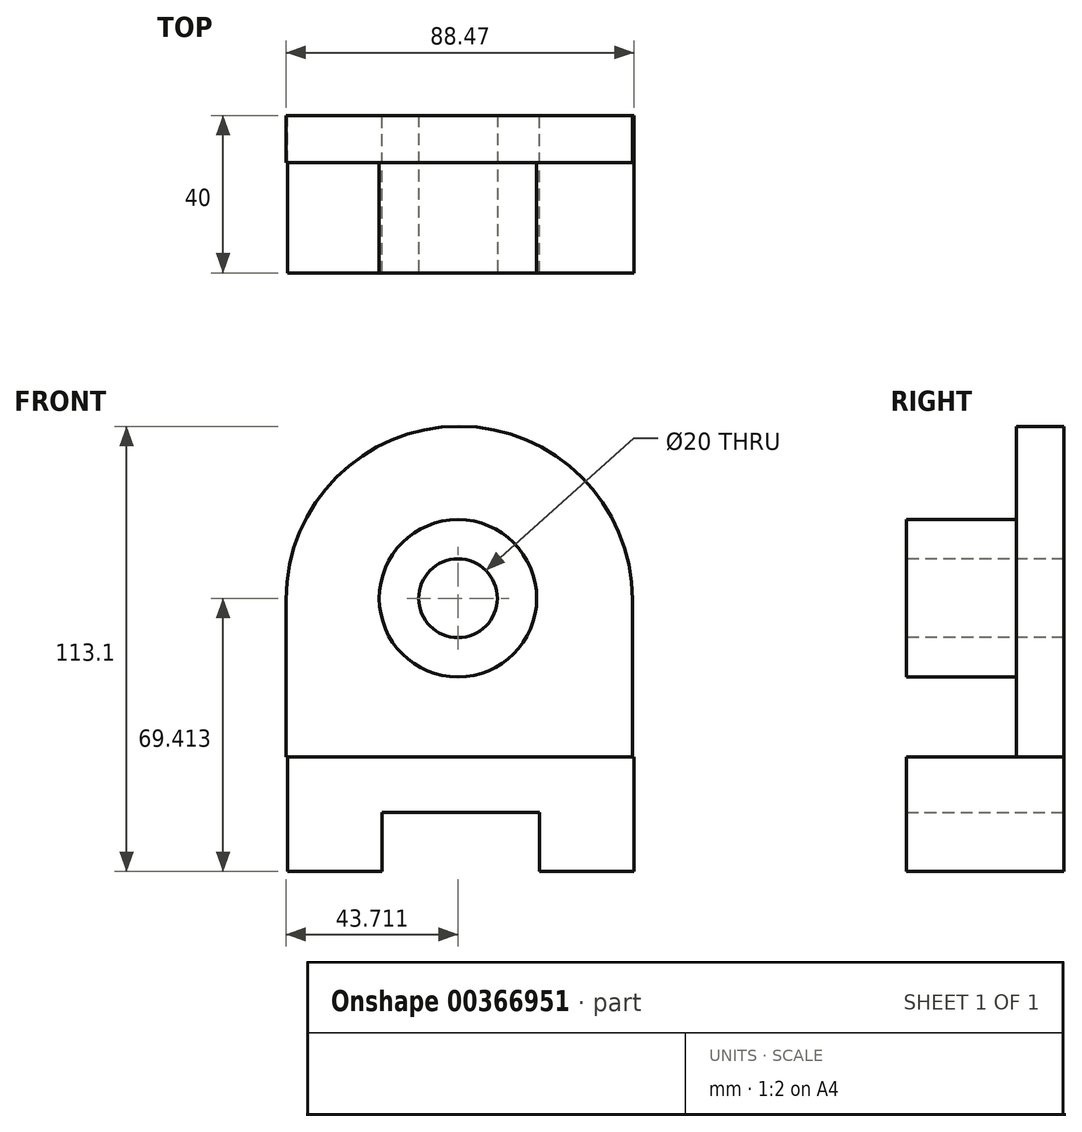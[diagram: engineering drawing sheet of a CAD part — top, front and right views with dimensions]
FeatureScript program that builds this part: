
annotation { "Feature Type Name" : "Feature", "Feature Type Description" : "" }
export const myFeature = defineFeature(function(context is Context, id is Id, definition is map)
    precondition{}
    {
        {
            var Q0;
            Q0=qCreatedBy(makeId("Front.planeOp"),FACE);
            var sketch = newSketch(context, id + "F0", { "sketchPlane" : qUnion([Q0])});
            skArc(sketch, "E0", {"start": v(44, 40) * mm, "mid": v(0, 84) * mm, "end": v(-44, 40) * mm});
            skLineSegment(sketch, "E1", {"start": v(-44, 0) * mm, "end": v(44, 0) * mm});
            skLineSegment(sketch, "E2", {"start": v(-44, 40) * mm, "end": v(-44, 0) * mm});
            skLineSegment(sketch, "E3", {"start": v(44, 40) * mm, "end": v(44, 0) * mm});
            skSolve(sketch);
        }
        {
            var Q0;
            Q0=qSketchRegion(id+"F0",true);
            extrude(context, id + "F1", {"entities" : qUnion([Q0]), "depth" : 12 * mm});
        }
        {
            var Q0;
            Q0=makeQuery(id+"F1.opExtrude","CAP_FACE",FACE,{"disambiguationData":[OSD([sQuery(id+"F0.wireOp",EDGE,"E0"),sQuery(id+"F0.wireOp",EDGE,"E1"),sQuery(id+"F0.wireOp",EDGE,"E2"),sQuery(id+"F0.wireOp",EDGE,"E3")])],"isStart":false});
            var sketch = newSketch(context, id + "F2", { "sketchPlane" : qUnion([Q0])});
            skCircle(sketch, "E4", {"center": v(-0.29, 40.31) * mm, "radius": 20 * mm});
            skSolve(sketch);
        }
        {
            var Q0;
            Q0=makeQuery(id+"F2.imprint","IMPRINT",FACE,{"disambiguationData":[TD([[makeQuery(id+"F2.imprint","IMPRINT",EDGE,{"derivedFrom":sQuery(id+"F2.wireOp",EDGE,"E4")}),1.0]])]});
            extrude(context, id + "F3", {"entities" : qUnion([Q0]), "operationType" : NewBodyOperationType.ADD, "depth" : 28 * mm});
        }
        {
            var Q0;
            Q0=qCreatedBy(makeId("Front.planeOp"),FACE);
            var sketch = newSketch(context, id + "F4", { "sketchPlane" : qUnion([Q0])});
            skLineSegment(sketch, "E5", {"start": v(44.47, 0) * mm, "end": v(44.47, -29.1) * mm});
            skLineSegment(sketch, "E6", {"start": v(44.47, -29.1) * mm, "end": v(20.47, -29.1) * mm});
            skLineSegment(sketch, "E7", {"start": v(20.47, -29.1) * mm, "end": v(20.47, -14.1) * mm});
            skLineSegment(sketch, "E8", {"start": v(20.47, -14.1) * mm, "end": v(-19.53, -14.1) * mm});
            skLineSegment(sketch, "E9", {"start": v(-19.53, -14.1) * mm, "end": v(-19.53, -29.1) * mm});
            skLineSegment(sketch, "E10", {"start": v(-19.53, -29.1) * mm, "end": v(-43.53, -29.1) * mm});
            skLineSegment(sketch, "E11", {"start": v(-43.53, -29.1) * mm, "end": v(-43.53, 0) * mm});
            skLineSegment(sketch, "E12", {"start": v(-43.53, 0) * mm, "end": v(44.47, 0) * mm});
            skSolve(sketch);
        }
        {
            var Q0;
            Q0=makeQuery(id+"F4.imprint","IMPRINT",FACE,{"disambiguationData":[TD([[makeQuery(id+"F4.imprint","IMPRINT",EDGE,{"derivedFrom":sQuery(id+"F4.wireOp",EDGE,"E5")}),-1.0]])]});
            extrude(context, id + "F5", {"entities" : qUnion([Q0]), "operationType" : NewBodyOperationType.ADD, "depth" : 40 * mm});
        }
        {
            var Q0;
            Q0=makeQuery(id+"F3.opExtrude","CAP_FACE",FACE,{"disambiguationData":[OSD([sQuery(id+"F2.wireOp",EDGE,"E4")])],"isStart":false});
            var sketch = newSketch(context, id + "F6", { "sketchPlane" : qUnion([Q0])});
            skCircle(sketch, "E13", {"center": v(-0.29, 40.31) * mm, "radius": 10 * mm});
            skSolve(sketch);
        }
        {
            var Q0;
            Q0=qSketchRegion(id+"F6",true);
            extrude(context, id + "F7", {"entities" : qUnion([Q0]), "operationType" : NewBodyOperationType.REMOVE, "oppositeDirection" : true, "depth" : 70 * mm});
        }
    });
